# Revit family: VTi.905.I_Фитинг_Вставка переходная_Нерж_VALTEC
name_source: partatom
category: Соединительные детали трубопроводов
units: mm (PartAtom-declared; Revit-internal decimal feet)

## family parameters
Всегда вертикально = Да
На основе рабочей плоскости = Нет
Общий = Нет
При загрузке вырезать с полостями = Нет
Размер круглого соединителя = Использовать радиус
Тип детали = Переход

## types (14) — shared parameters
ADSK_Единица измерения = шт.
ADSK_Количество = 1
ADSK_Материал = Сталь, нержавеющая - VALTEC
LT = VTi.905.I_Фитинг_Вставка переходная_Нерж_VALTEC
zero-valued in all types: Отметка по умолчанию

## type names (no varying parameters)
- Фитинг из нержавеющей стали - вставка переходная 18х15 мм
- Фитинг из нержавеющей стали - вставка переходная 22х15 мм
- Фитинг из нержавеющей стали - вставка переходная 22х18 мм
- Фитинг из нержавеющей стали - вставка переходная 28х15 мм
- Фитинг из нержавеющей стали - вставка переходная 28х18 мм
- Фитинг из нержавеющей стали - вставка переходная 28х22 мм
- Фитинг из нержавеющей стали - вставка переходная 35х15 мм
- Фитинг из нержавеющей стали - вставка переходная 35х18 мм
- Фитинг из нержавеющей стали - вставка переходная 35х22 мм
- Фитинг из нержавеющей стали - вставка переходная 35х28 мм
- Фитинг из нержавеющей стали - вставка переходная 42х22 мм
- Фитинг из нержавеющей стали - вставка переходная 42х28 мм
- Фитинг из нержавеющей стали - вставка переходная 42х35 мм
- Фитинг из нержавеющей стали - вставка переходная 54х28 мм
